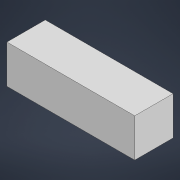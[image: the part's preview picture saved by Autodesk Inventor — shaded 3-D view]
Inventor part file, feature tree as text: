
AUTODESK INVENTOR PART (.ipt)
format: ipt  version: 2022 (Build 260153000, 153)  size: 197,120 bytes
history: native  units: in
note: dims shown in document units (in); Inventor stores cm internally (conversion verified against a paired STEP export)
features: extrude x1, sketch x1
ambient origin geometry x8: Origin, YZ Plane, XZ Plane, XY Plane, X Axis, Y Axis, Z Axis, Center Point
bodies: Solid1 (feature_tree)
feature tree (2):
  extrude  "Extrusion1"  Depth=0.075in
  sketch  "Sketch1"  dims[d0=0.25in d1=0.075in d2=0.075in d3=0.0in]
